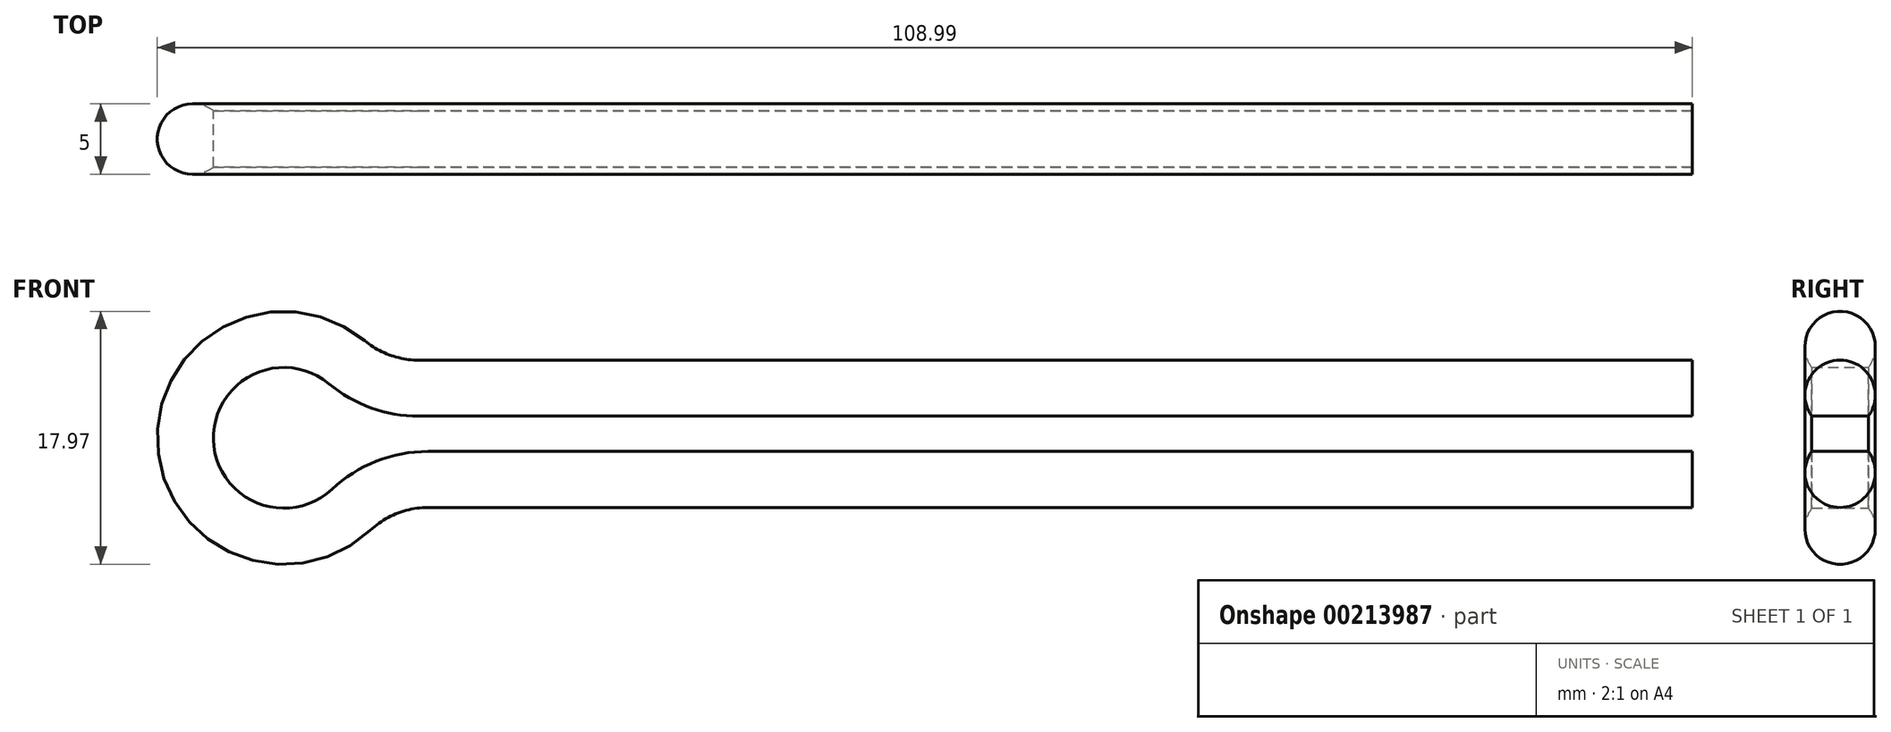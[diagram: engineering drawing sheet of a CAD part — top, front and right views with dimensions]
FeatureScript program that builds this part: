
annotation { "Feature Type Name" : "Feature", "Feature Type Description" : "" }
export const myFeature = defineFeature(function(context is Context, id is Id, definition is map)
    precondition{}
    {
        {
            var Q0;
            Q0=qCreatedBy(makeId("Front.planeOp"),FACE);
            var sketch = newSketch(context, id + "F0", { "sketchPlane" : qUnion([Q0])});
            skLineSegment(sketch, "E0", {"start": v(0, 0) * mm, "end": v(-89.76, 0) * mm});
            skLineSegment(sketch, "E1", {"start": v(0, 2.5) * mm, "end": v(-90.41, 2.5) * mm});
            skArc(sketch, "E2", {"start": v(-96.8, 4.8) * mm, "mid": v(-105, 0.82) * mm, "end": v(-96.59, -2.7) * mm});
            skPoint(sketch, "E3.visualSharp", {"position": v(-95.24, 2.5) * mm});
            skArc(sketch, "E3.filletArc", {"start": v(-96.8, 4.8) * mm, "mid": v(-93.81, 3.1) * mm, "end": v(-90.41, 2.5) * mm});
            skPoint(sketch, "E4.visualSharp", {"position": v(-95.1, 0) * mm});
            skArc(sketch, "E4.filletArc", {"start": v(-89.76, 0) * mm, "mid": v(-93.43, -0.7) * mm, "end": v(-96.59, -2.7) * mm});
            skSolve(sketch);
        }
        {
            var Q0;
            Q0=qCreatedBy(makeId("Right.planeOp"),FACE);
            var sketch = newSketch(context, id + "F1", { "sketchPlane" : qUnion([Q0])});
            skLineSegment(sketch, "E5", {"start": v(2, 0) * mm, "end": v(-2, 0) * mm});
            skArc(sketch, "E6", {"start": v(-2, 0) * mm, "mid": v(0, -3.99) * mm, "end": v(2, 0) * mm});
            skSolve(sketch);
        }
        {
            var Q0;
            Q0 = qSketchRegion(id + "F1", true);
            var Q1;
            Q1 = qConstructionFilter(qBodyType(qCreatedBy(id + "F0" ,EDGE), BodyType.WIRE), ConstructionObject.NO);
            sweep(context, id + "F2", {"profiles" : qUnion([Q0]), "path" : qUnion([Q1])});
        }
    });
